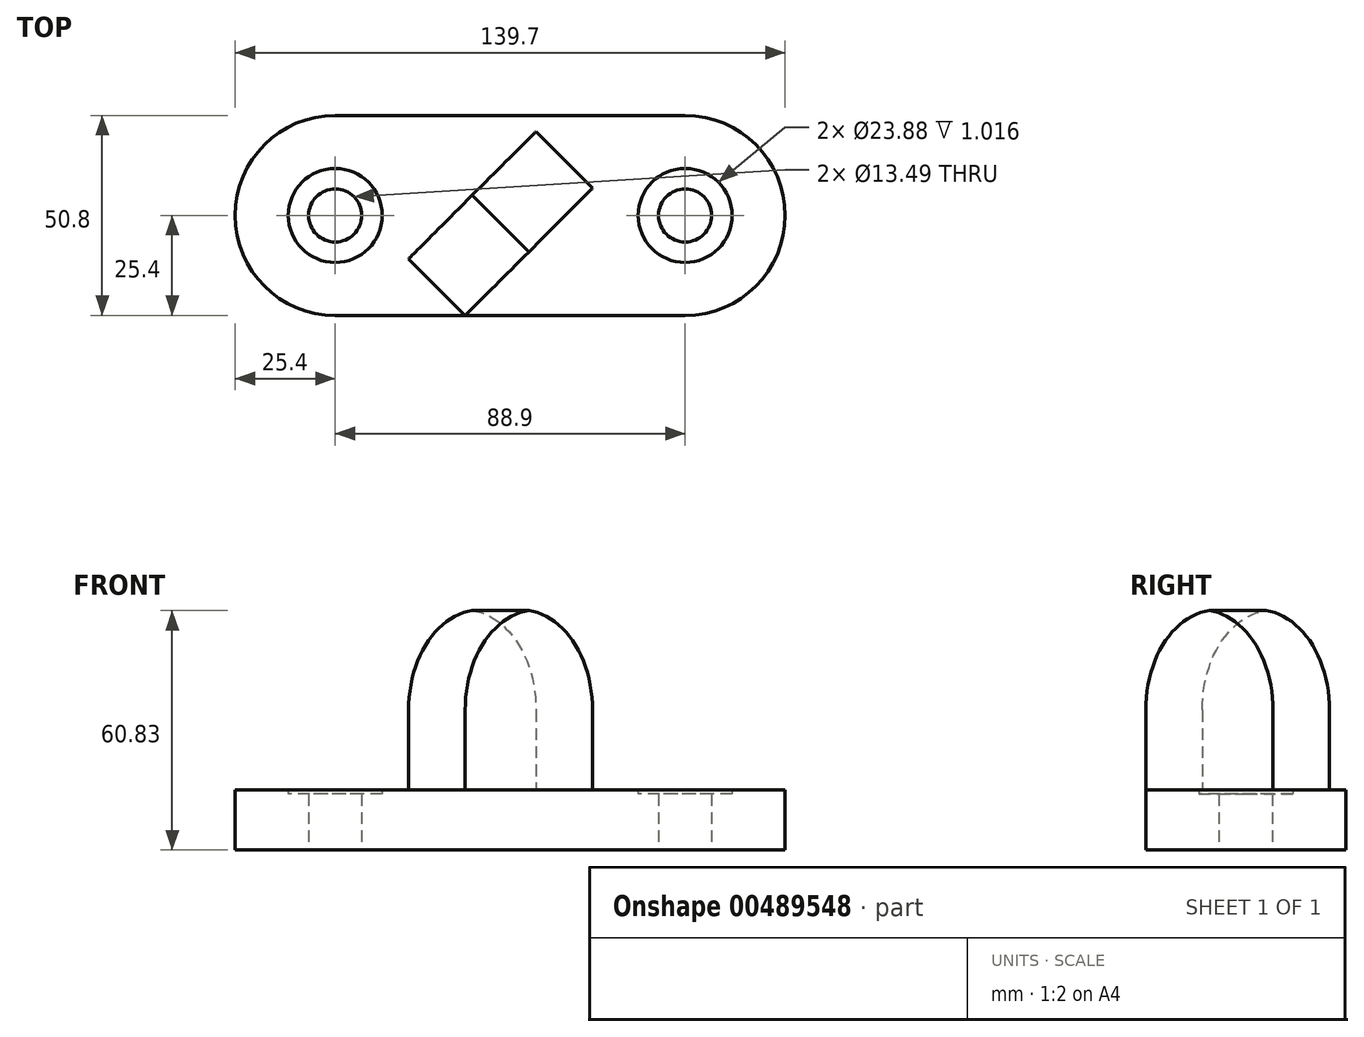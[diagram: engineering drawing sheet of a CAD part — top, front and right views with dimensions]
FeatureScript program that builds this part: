
annotation { "Feature Type Name" : "Feature", "Feature Type Description" : "" }
export const myFeature = defineFeature(function(context is Context, id is Id, definition is map)
    precondition{}
    {
        {
            var Q0;
            Q0=qCreatedBy(makeId("Top.planeOp"),FACE);
            var sketch = newSketch(context, id + "F0", { "sketchPlane" : qUnion([Q0])});
            skLineSegment(sketch, "E0.bottom", {"start": v(44.45, 25.4) * mm, "end": v(-44.45, 25.4) * mm});
            skLineSegment(sketch, "E0.top", {"start": v(44.45, -25.4) * mm, "end": v(-44.45, -25.4) * mm});
            skPoint(sketch, "E0.middle", {"position": v(0, 0) * mm});
            skArc(sketch, "E1", {"start": v(-44.45, 25.4) * mm, "mid": v(-69.85, 0) * mm, "end": v(-44.45, -25.4) * mm});
            skArc(sketch, "E2", {"start": v(44.45, -25.4) * mm, "mid": v(69.85, 0) * mm, "end": v(44.45, 25.4) * mm});
            skCircle(sketch, "E3", {"center": v(-44.45, 0) * mm, "radius": 11.94 * mm});
            skCircle(sketch, "E4", {"center": v(44.45, 0) * mm, "radius": 11.94 * mm});
            skCircle(sketch, "E5", {"center": v(-44.45, 0) * mm, "radius": 6.74 * mm});
            skCircle(sketch, "E6", {"center": v(44.45, 0) * mm, "radius": 6.74 * mm});
            skPoint(sketch, "E7", {"position": v(-11.43, -25.4) * mm});
            skSolve(sketch);
        }
        {
            var Q0;
            Q0 = qSketchRegion(id + "F0", true);
            extrude(context, id + "F1", {"entities" : qUnion([Q0]), "depth" : 15.24 * mm});
        }
        {
            var Q0;
            Q0=makeQuery(id+"F0.imprint","IMPRINT",FACE,{"disambiguationData":[TD([[makeQuery(id+"F0.imprint","IMPRINT",EDGE,{"derivedFrom":sQuery(id+"F0.wireOp",EDGE,"E3")}),1.0]])]});
            var Q1;
            Q1=makeQuery(id+"F0.imprint","IMPRINT",FACE,{"disambiguationData":[TD([[makeQuery(id+"F0.imprint","IMPRINT",EDGE,{"derivedFrom":sQuery(id+"F0.wireOp",EDGE,"E4")}),1.0]])]});
            extrude(context, id + "F2", {"entities" : qUnion([Q0, Q1]), "operationType" : NewBodyOperationType.ADD, "depth" : 14.22 * mm});
        }
        {
            var Q0;
            Q0=qCreatedBy(makeId("Front.planeOp"),FACE);
            var sketch = newSketch(context, id + "F3", { "sketchPlane" : qUnion([Q0])});
            skLineSegment(sketch, "E8", {"start": v(0, 0) * mm, "end": v(0, 50.27) * mm, "construction": true});
            skSolve(sketch);
        }
        {
            var Q0;
            Q0=makeQuery(id+"F1.opExtrude","CAP_FACE",FACE,{"disambiguationData":[OSD([sQuery(id+"F0.wireOp",EDGE,"E0.bottom"),sQuery(id+"F0.wireOp",EDGE,"E0.top"),sQuery(id+"F0.wireOp",EDGE,"E1"),sQuery(id+"F0.wireOp",EDGE,"E2"),sQuery(id+"F0.wireOp",EDGE,"E3"),sQuery(id+"F0.wireOp",EDGE,"E4")])],"isStart":false});
            var sketch = newSketch(context, id + "F4", { "sketchPlane" : qUnion([Q0])});
            skPoint(sketch, "E9.0", {"position": v(-11.43, -25.4) * mm});
            skLineSegment(sketch, "E10", {"start": v(-11.43, -25.4) * mm, "end": v(20.9, 6.93) * mm});
            skLineSegment(sketch, "E11", {"start": v(-11.43, -25.4) * mm, "end": v(-25.8, -11.03) * mm});
            skLineSegment(sketch, "E12", {"start": v(-25.8, -11.03) * mm, "end": v(6.53, 21.3) * mm});
            skLineSegment(sketch, "E13", {"start": v(6.53, 21.3) * mm, "end": v(20.9, 6.93) * mm});
            skSolve(sketch);
        }
        {
            var Q0;
            Q0=makeQuery(id+"F4.imprint","IMPRINT",FACE,{"disambiguationData":[TD([[makeQuery(id+"F4.imprint","IMPRINT",EDGE,{"derivedFrom":sQuery(id+"F4.wireOp",EDGE,"E10")}),1.0]])]});
            extrude(context, id + "F5", {"entities" : qUnion([Q0]), "operationType" : NewBodyOperationType.ADD, "depth" : 45.72 * mm});
        }
        {
            var Q0;
            Q0=makeQuery(id+"F5.opExtrude","CAP_EDGE",EDGE,{"disambiguationData":[OSD([sQuery(id+"F4.wireOp",EDGE,"E11")])],"isStart":false});
            var Q1;
            Q1=makeQuery(id+"F5.opExtrude","CAP_EDGE",EDGE,{"disambiguationData":[OSD([sQuery(id+"F4.wireOp",EDGE,"E13")])],"isStart":false});
            fillet(context, id + "F6", {"entities" : qUnion([Q0, Q1]), "radius" : 25.4 * mm, "tangentPropagation" : true, "allowEdgeOverflow" : false});
        }
    });
